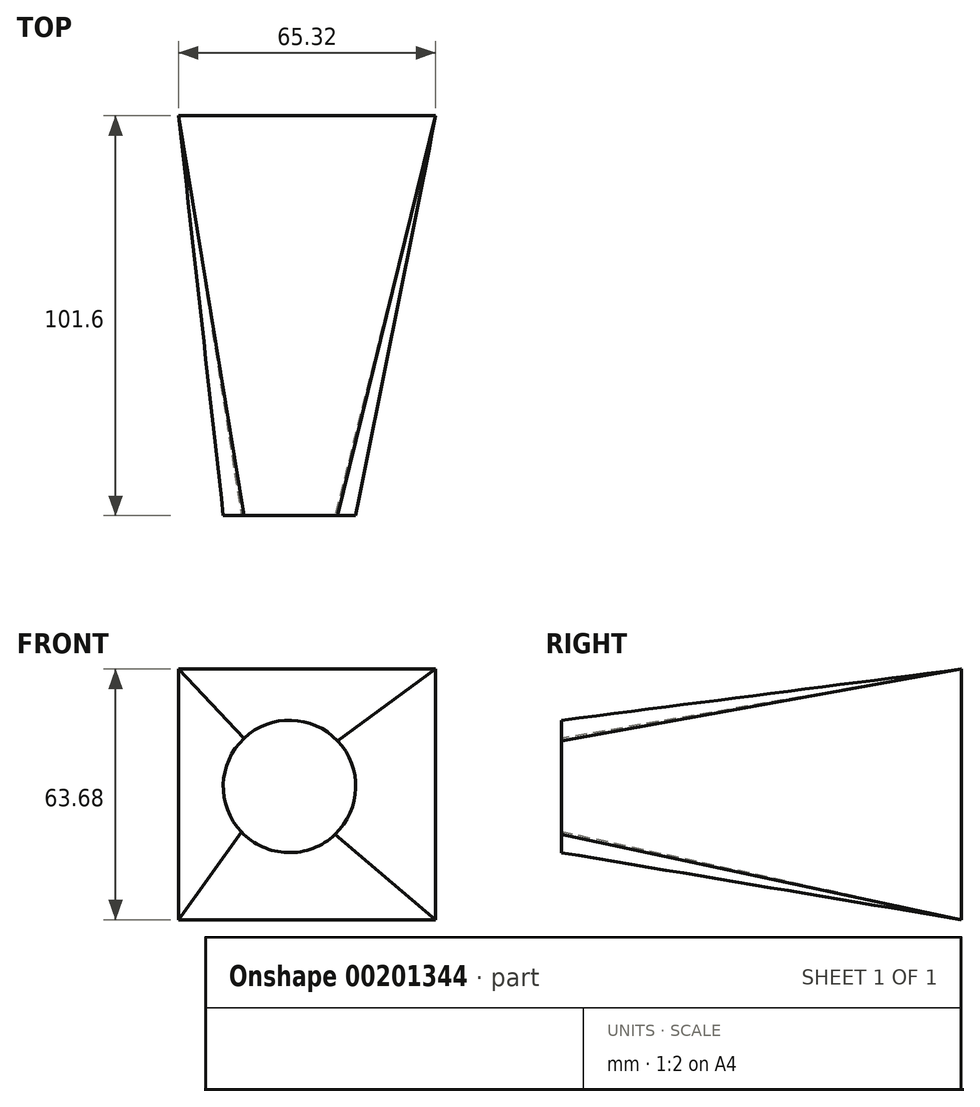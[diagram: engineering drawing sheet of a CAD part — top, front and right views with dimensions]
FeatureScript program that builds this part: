
annotation { "Feature Type Name" : "Feature", "Feature Type Description" : "" }
export const myFeature = defineFeature(function(context is Context, id is Id, definition is map)
    precondition{}
    {
        {
            var Q0;
            Q0=qCreatedBy(makeId("Front.planeOp"),FACE);
            var sketch = newSketch(context, id + "F0", { "sketchPlane" : qUnion([Q0])});
            skLineSegment(sketch, "E0.bottom", {"start": v(-28.17, 29.8) * mm, "end": v(37.15, 29.8) * mm});
            skLineSegment(sketch, "E0.top", {"start": v(-28.17, -33.88) * mm, "end": v(37.15, -33.88) * mm});
            skLineSegment(sketch, "E0.left", {"start": v(-28.17, 29.8) * mm, "end": v(-28.17, -33.88) * mm});
            skLineSegment(sketch, "E0.right", {"start": v(37.15, 29.8) * mm, "end": v(37.15, -33.88) * mm});
            skSolve(sketch);
        }
        {
            var Q0;
            Q0=qCreatedBy(makeId("Front.planeOp"),FACE);
            cPlane(context, id + "F1", {"entities" : qUnion([Q0]), "cplaneType" : CPlaneType.OFFSET, "offset" : 101.6 * mm, "width" : 152.4 * mm, "height" : 152.4 * mm});
        }
        {
            var Q0;
            Q0=qCreatedBy(id+"F1.planeOp",FACE);
            var sketch = newSketch(context, id + "F2", { "sketchPlane" : qUnion([Q0])});
            skCircle(sketch, "E1", {"center": v(0, 0) * mm, "radius": 16.83 * mm});
            skSolve(sketch);
        }
        {
            var Q0;
            Q0=makeQuery(id+"F0.imprint","IMPRINT",FACE,{"disambiguationData":[TD([[makeQuery(id+"F0.imprint","IMPRINT",EDGE,{"derivedFrom":sQuery(id+"F0.wireOp",EDGE,"E0.bottom")}),-1.0]])]});
            var Q1;
            Q1=makeQuery(id+"F2.imprint","IMPRINT",FACE,{"disambiguationData":[TD([[makeQuery(id+"F2.imprint","IMPRINT",EDGE,{"derivedFrom":sQuery(id+"F2.wireOp",EDGE,"E1")}),1.0]])]});
            loft(context, id + "F3", {"sheetProfilesArray" : [{ "sheetProfileEntities" : qUnion([Q0]) }, { "sheetProfileEntities" : qUnion([Q1]) }]});
        }
    });
